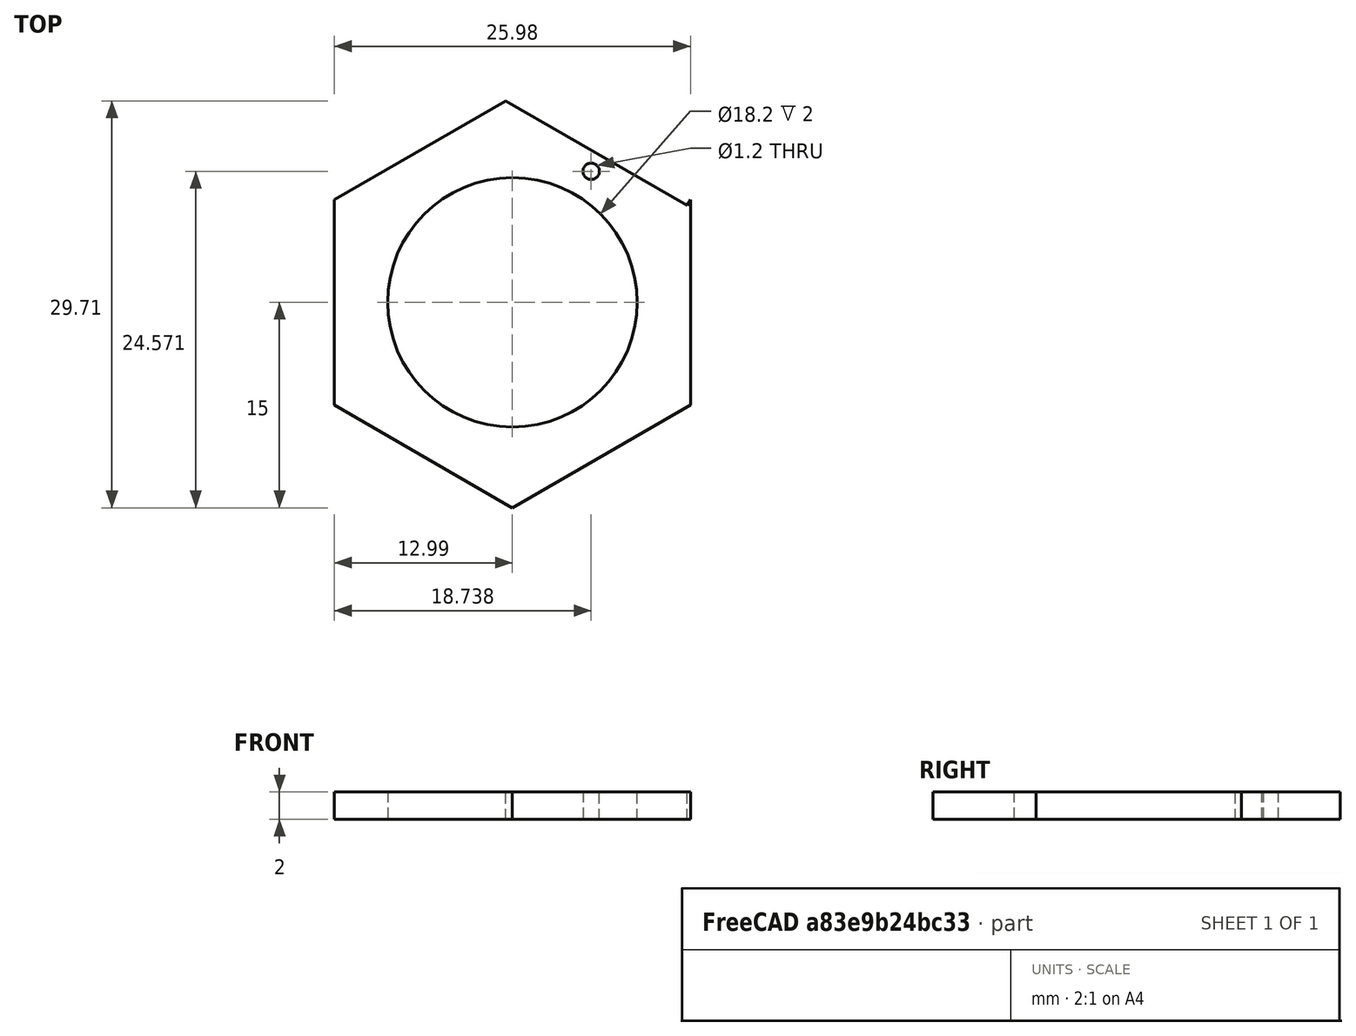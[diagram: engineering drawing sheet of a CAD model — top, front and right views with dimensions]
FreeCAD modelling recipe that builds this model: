
FCSTD DOCUMENT  (FreeCAD 0.21R33771 (Git))
Label: internal_centring_bulkhead
License: All rights reserved
LicenseURL: http://en.wikipedia.org/wiki/All_rights_reserved
objects: Sketcher::SketchObject×1, PartDesign::Pad×1, PartDesign::Body×1
note: 4 computed .brp shape members not serialized (recipe doc carries the construction recipe); baked Part::Feature solids carry a one-line shape summary decoded from their .brp

FEATURE [Sketcher::SketchObject] Sketch
  FullyConstrained = false
  MapMode = 5
  Support = -> [XY_Plane]
  sketch-geometry (10):
    g0: LineSegment StartX=-0.50397 StartY=14.7134 StartZ=0 EndX=-12.9849 EndY=7.50882 EndZ=0
    g1: LineSegment StartX=-12.9849 StartY=7.50882 StartZ=0 EndX=-12.99 EndY=-7.5 EndZ=0
    g2: LineSegment StartX=-12.99 StartY=-7.5 StartZ=0 EndX=0 EndY=-14.9997 EndZ=0
    g3: LineSegment StartX=0 StartY=-14.9997 StartZ=0 EndX=12.99 EndY=-7.5 EndZ=0
    g4: LineSegment StartX=12.99 StartY=-7.5 StartZ=0 EndX=12.99 EndY=7.5 EndZ=0
    g5: Circle CenterX=0 CenterY=0 CenterZ=0 NormalX=0 NormalY=0 NormalZ=1 AngleXU=0 Radius=14.9997
    g6: LineSegment StartX=-0.50397 StartY=14.7134 StartZ=0 EndX=12.74 EndY=7.06699 EndZ=0
    g7: LineSegment StartX=12.74 StartY=7.06699 StartZ=0 EndX=12.99 EndY=7.5 EndZ=0
    g8: Circle CenterX=0 CenterY=0 CenterZ=0 NormalX=0 NormalY=0 NormalZ=1 AngleXU=0 Radius=9.1
    g9: Circle CenterX=5.74772 CenterY=9.57141 CenterZ=0 NormalX=0 NormalY=0 NormalZ=1 AngleXU=0 Radius=0.6
  constraints (22):
    c: Coincident(g0,g1)
    c: Coincident(g1,g2)
    c: Coincident(g2,g3)
    c: Coincident(g3,g4)
    c: PointOnObject(g0,g5)
    c: PointOnObject(g1,g5)
    c: PointOnObject(g2,g5)
    c: PointOnObject(g3,g5)
    c: PointOnObject(g4,g5)
    c: Coincident(g5,g-1)
    c: Coincident(g6,g7)
    c: Coincident(g7,g4)
    c: Vertical(g4)
    c: Angle(g7,g4) = 0.523599
    c: Distance(g7) = 0.5
    c: Coincident(g8,g5)
    c: Radius(g8) = 9.1
    c: Angle(g7,g6) = 1.5708
    c: DistanceX(g8,g4) = 12.99
    c: DistanceY(g8,g4) = 7.5
    c: Coincident(g0,g6)
    c: Radius(g9) = 0.6
FEATURE [PartDesign::Pad] Pad
  Direction = (0,0,1)
  Length = 2
  Length2 = 10
  Profile = -> Sketch
  ReferenceAxis = -> Sketch [N_Axis]
  Type = 0
FEATURE [PartDesign::Body] Body
  Group = -> [Sketch,Pad]
  Origin = -> Origin
  Tip = -> Pad
